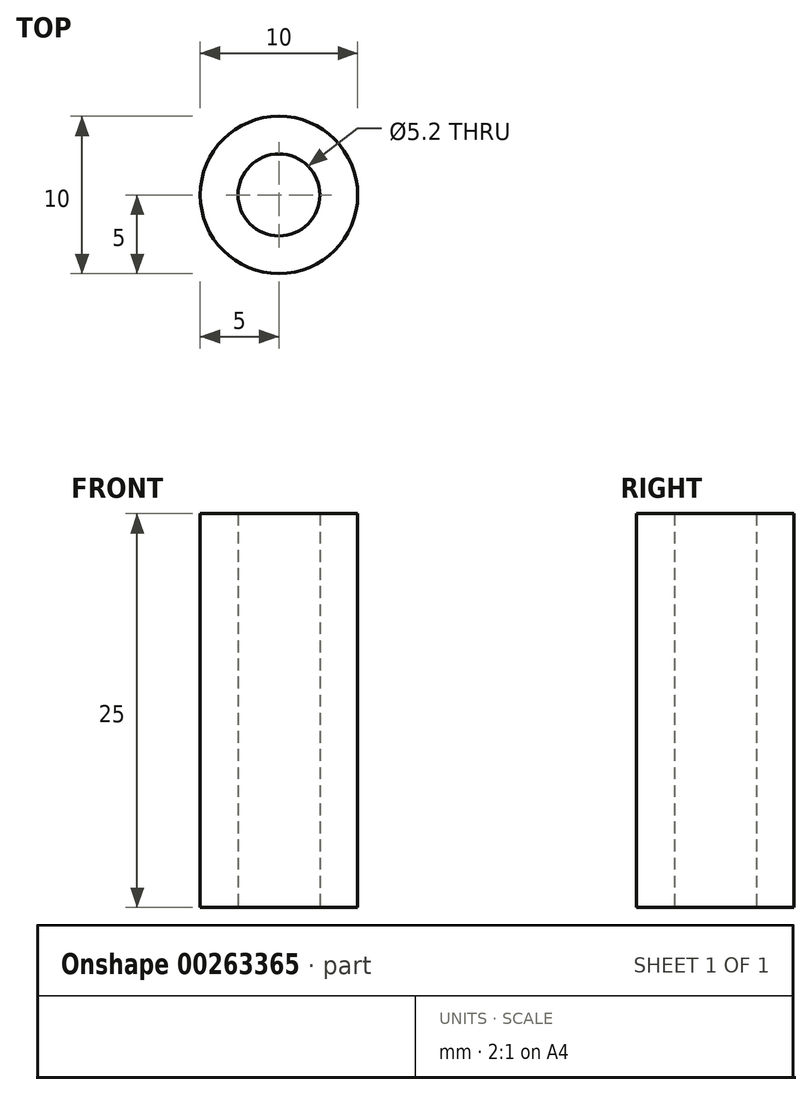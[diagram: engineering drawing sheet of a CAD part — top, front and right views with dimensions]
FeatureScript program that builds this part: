
annotation { "Feature Type Name" : "Feature", "Feature Type Description" : "" }
export const myFeature = defineFeature(function(context is Context, id is Id, definition is map)
    precondition{}
    {
        {
            var Q0;
            Q0=qCreatedBy(makeId("Top.planeOp"),FACE);
            var sketch = newSketch(context, id + "F0", { "sketchPlane" : qUnion([Q0])});
            skCircle(sketch, "E0", {"center": v(0, 0) * mm, "radius": 5 * mm});
            skCircle(sketch, "E1", {"center": v(0, 0) * mm, "radius": 2.6 * mm});
            skSolve(sketch);
        }
        {
            var Q0;
            Q0=makeQuery(id+"F0.imprint","IMPRINT",FACE,{"disambiguationData":[TD([[makeQuery(id+"F0.imprint","IMPRINT",EDGE,{"derivedFrom":sQuery(id+"F0.wireOp",EDGE,"E0")}),1.0]])]});
            extrude(context, id + "F1", {"entities" : qUnion([Q0]), "depth" : 25 * mm});
        }
    });
